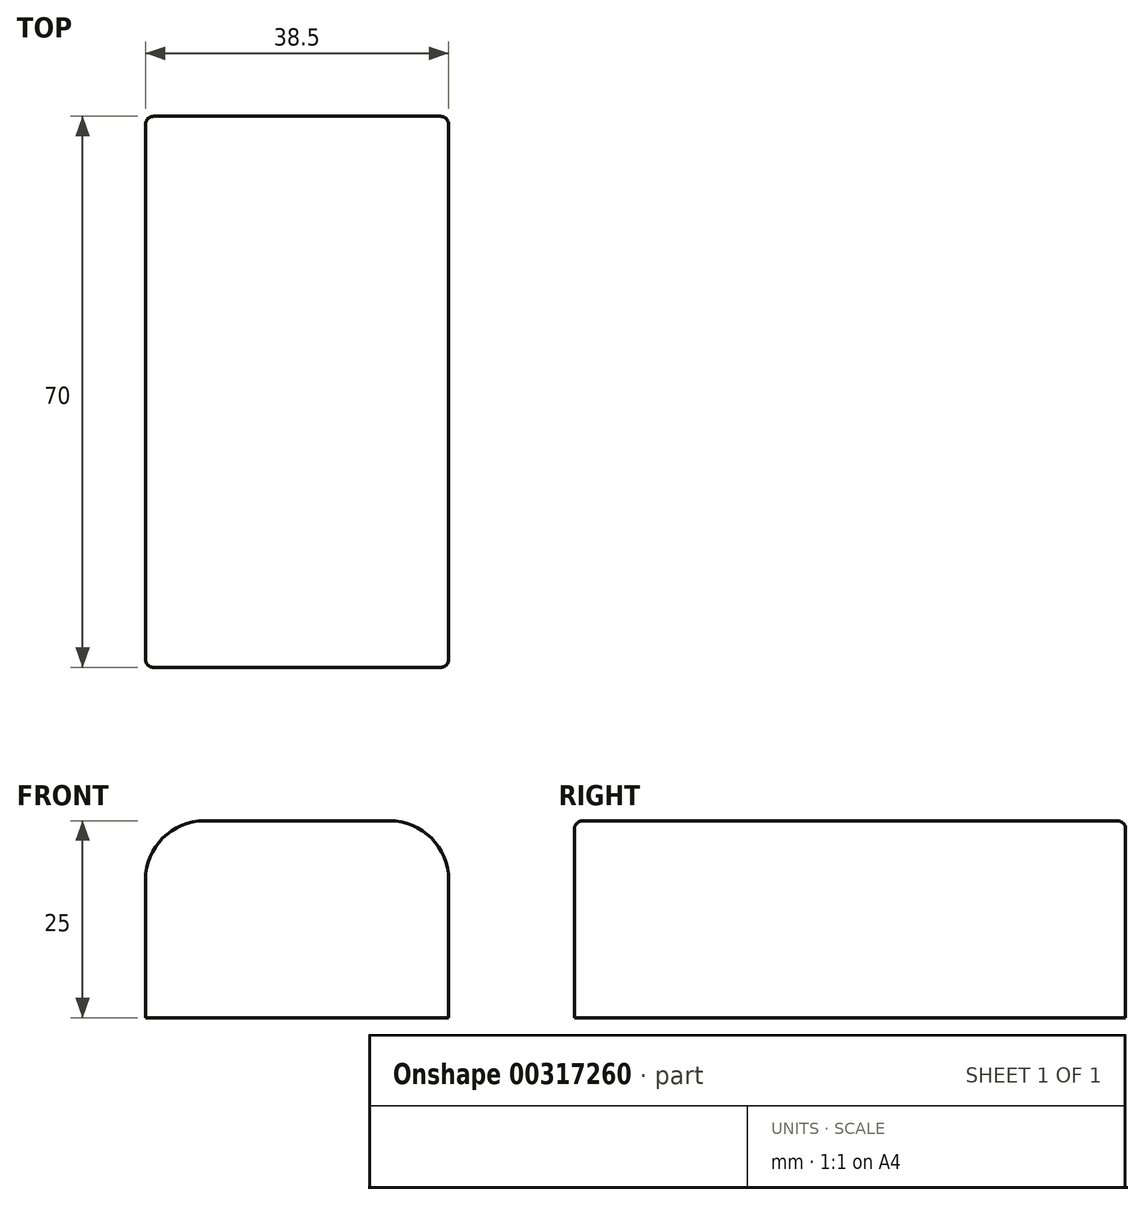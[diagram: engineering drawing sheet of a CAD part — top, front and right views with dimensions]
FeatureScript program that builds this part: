
annotation { "Feature Type Name" : "Feature", "Feature Type Description" : "" }
export const myFeature = defineFeature(function(context is Context, id is Id, definition is map)
    precondition{}
    {
        {
            var Q0;
            Q0=qCreatedBy(makeId("Top.planeOp"),FACE);
            var sketch = newSketch(context, id + "F0", { "sketchPlane" : qUnion([Q0])});
            skLineSegment(sketch, "E0.bottom", {"start": v(19.25, -35) * mm, "end": v(-19.25, -35) * mm});
            skLineSegment(sketch, "E0.top", {"start": v(19.25, 35) * mm, "end": v(-19.25, 35) * mm});
            skLineSegment(sketch, "E0.left", {"start": v(19.25, -35) * mm, "end": v(19.25, 35) * mm});
            skLineSegment(sketch, "E0.right", {"start": v(-19.25, -35) * mm, "end": v(-19.25, 35) * mm});
            skPoint(sketch, "E0.middle", {"position": v(0, 0) * mm});
            skSolve(sketch);
        }
        {
            var Q0;
            Q0=makeQuery(id+"F0.imprint","IMPRINT",FACE,{"disambiguationData":[TD([[makeQuery(id+"F0.imprint","IMPRINT",EDGE,{"derivedFrom":sQuery(id+"F0.wireOp",EDGE,"E0.bottom")}),-1.0]])]});
            extrude(context, id + "F1", {"entities" : qUnion([Q0]), "depth" : 25 * mm});
        }
        {
            var Q0;
            Q0=makeQuery(id+"F1.opExtrude","CAP_EDGE",EDGE,{"disambiguationData":[OSD([sQuery(id+"F0.wireOp",EDGE,"E0.left")])],"isStart":false});
            var Q1;
            Q1=makeQuery(id+"F1.opExtrude","CAP_EDGE",EDGE,{"disambiguationData":[OSD([sQuery(id+"F0.wireOp",EDGE,"E0.right")])],"isStart":false});
            fillet(context, id + "F2", {"entities" : qUnion([Q0, Q1]), "radius" : 7.5 * mm, "tangentPropagation" : true, "allowEdgeOverflow" : false});
        }
        {
            var Q0;
            Q0=makeQuery(id+"F1.opExtrude","SWEPT_EDGE",EDGE,{"disambiguationData":[OSD([sQuery(id+"F0.wireOp",EDGE,"E0.bottom"),sQuery(id+"F0.wireOp",EDGE,"E0.left")])]});
            var Q1;
            Q1=makeQuery(id+"F1.opExtrude","SWEPT_EDGE",EDGE,{"disambiguationData":[OSD([sQuery(id+"F0.wireOp",EDGE,"E0.top"),sQuery(id+"F0.wireOp",EDGE,"E0.left")])]});
            fillet(context, id + "F3", {"entities" : qUnion([Q0, Q1]), "radius" : 1 * mm, "tangentPropagation" : true, "allowEdgeOverflow" : false});
        }
    });
